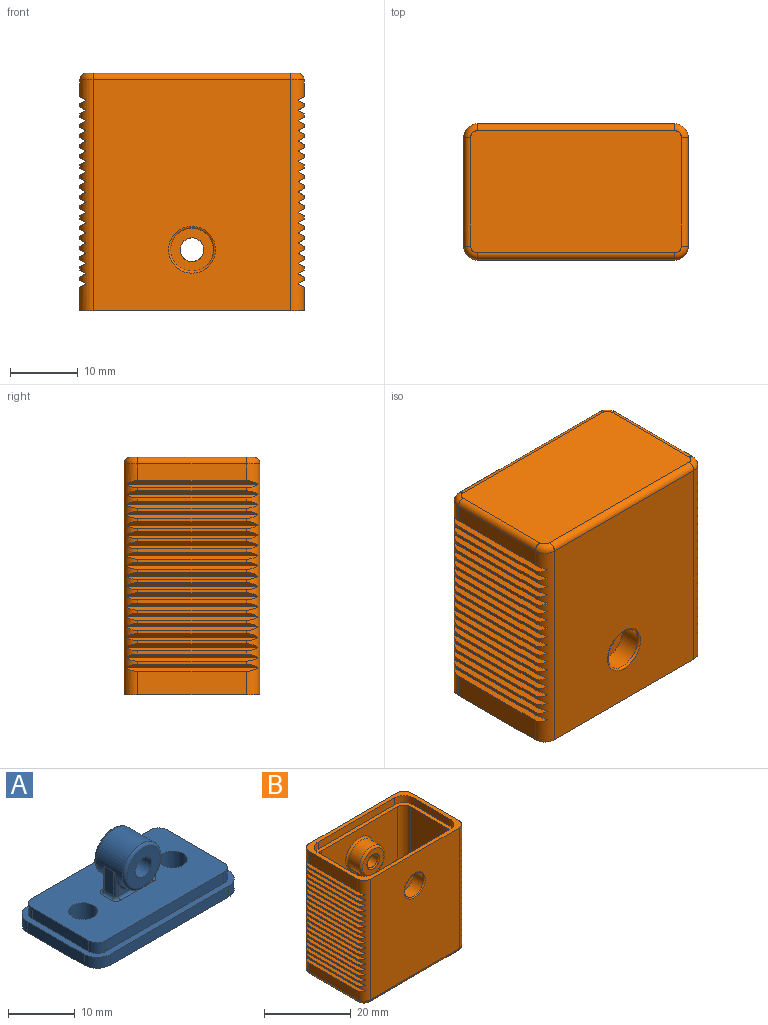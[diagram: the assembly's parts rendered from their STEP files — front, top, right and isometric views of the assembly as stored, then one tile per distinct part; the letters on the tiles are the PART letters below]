
ASSEMBLY  parts=2 mates=1
PART A: 51 faces, bbox 30.6x17.6x13.3 mm
  f0: plane 3.5x1.67mm, normal (0,-1,0), area 1.8mm2, adj f32,f40,f41
  f1: plane 3.5x1.67mm, normal (0,1,0), area 1.8mm2, adj f33,f42,f43
  f2: plane 28.6x15.6mm, normal (0,0,1), area 379.2mm2, adj f9,f10,f11,f12,f25,f26,f27,f28
  f3: plane 30.6x17.6mm, normal (0,0,1), area 88.5mm2, adj f4,f6,f7,f8,f9,f10,f11,f12
  f4: plane 12x2mm, normal (-1,0,0), area 24mm2, adj f3,f5,f21,f23
  f5: plane 30.6x17.6mm, normal (0,0,-1), area 502.8mm2, adj f4,f6,f7,f8,f21,f22,f23,f24
  f6: plane 12x2mm, normal (1,0,0), area 24mm2, adj f3,f5,f22,f24
  f7: plane 25x2mm, normal (0,-1,0), area 50mm2, adj f3,f5,f23,f24
  f8: plane 25x2mm, normal (0,1,0), area 50mm2, adj f3,f5,f21,f22
  f9: plane 12x2mm, normal (-1,0,0), area 24mm2, adj f2,f3,f25,f27
  f10: plane 12x2mm, normal (1,0,0), area 24mm2, adj f2,f3,f26,f28
  f11: plane 25x2mm, normal (0,-1,0), area 50mm2, adj f2,f3,f27,f28
  f12: plane 25x2mm, normal (0,1,0), area 50mm2, adj f2,f3,f25,f26
  f13: plane 4.5x2mm, normal (-1,0,0), area 9mm2, adj f18,f31,f34,f35
  f14: plane 4.5x2mm, normal (1,0,0), area 9mm2, adj f18,f41,f42,f46
  f15: plane 3.5x1.67mm, normal (0,-1,0), area 1.8mm2, adj f31,f32,f40
  f16: plane 3.5x1.67mm, normal (0,1,0), area 1.8mm2, adj f33,f34,f43
  f17: cylinder r=1.75mm len=6.6mm, axis (0,1,0), area 72.6mm2, adj f19,f20
  f18: cylinder r=4mm len=8mm, axis (0,1,0), area 94.7mm2, adj f13,f14,f29,f30,f32,f33,f37,f38
  f19: plane 7x7mm, normal (0,-1,0), area 28.9mm2, adj f17,f48
  f20: plane 7x7mm, normal (0,1,0), area 28.9mm2, adj f17,f47
  f21: cylinder r=2.8mm len=2.8mm, axis (0,0,-1), area 8.8mm2, adj f3,f4,f5,f8
  f22: cylinder r=2.8mm len=2.8mm, axis (0,0,1), area 8.8mm2, adj f3,f5,f6,f8
  f23: cylinder r=2.8mm len=2.8mm, axis (0,0,1), area 8.8mm2, adj f3,f4,f5,f7
  f24: cylinder r=2.8mm len=2.8mm, axis (0,0,-1), area 8.8mm2, adj f3,f5,f6,f7
  f25: cylinder r=1.8mm len=2mm, axis (0,0,-1), area 5.7mm2, adj f2,f3,f9,f12
  f26: cylinder r=1.8mm len=2mm, axis (0,0,1), area 5.7mm2, adj f2,f3,f10,f12
  f27: cylinder r=1.8mm len=2mm, axis (0,0,1), area 5.7mm2, adj f2,f3,f9,f11
  f28: cylinder r=1.8mm len=2mm, axis (0,0,-1), area 5.7mm2, adj f2,f3,f10,f11
  f29: bspline ~2.89x1mm, area 1.1mm2, adj f18,f31,f32
  f30: bspline ~2.89x1mm, area 1.1mm2, adj f18,f33,f34
  f31: cylinder r=0.5mm len=4.5mm, axis (0,0,1), area 2.3mm2, adj f13,f15,f29,f36
  f32: torus R=4.5mm, axis (0,-1,0), area 5.9mm2, adj f0,f15,f18,f29,f37
  f33: torus R=4.5mm, axis (0,-1,0), area 5.9mm2, adj f1,f16,f18,f30,f38
  f34: cylinder r=0.5mm len=4.5mm, axis (0,0,-1), area 2.3mm2, adj f13,f16,f30,f39
  f35: cylinder r=0.5mm len=2mm, axis (0,1,0), area 1.6mm2, adj f2,f13,f36,f39
  f36: torus R=1mm, axis (0,0,1), area 0.8mm2, adj f2,f31,f35,f40
  f37: bspline ~2.89x1mm, area 1.1mm2, adj f18,f32,f41
  f38: bspline ~2.89x1mm, area 1.1mm2, adj f18,f33,f42
  f39: torus R=1mm, axis (0,0,1), area 0.8mm2, adj f2,f34,f35,f43
  f40: cylinder r=0.5mm len=7mm, axis (-1,0,0), area 5.5mm2, adj f0,f2,f15,f36,f44
  f41: cylinder r=0.5mm len=4.5mm, axis (0,0,-1), area 2.3mm2, adj f0,f14,f37,f44
  f42: cylinder r=0.5mm len=4.5mm, axis (0,0,1), area 2.3mm2, adj f1,f14,f38,f45
  f43: cylinder r=0.5mm len=7mm, axis (1,0,0), area 5.5mm2, adj f1,f2,f16,f39,f45
  f44: torus R=1mm, axis (0,0,1), area 0.8mm2, adj f2,f40,f41,f46
  f45: torus R=1mm, axis (0,0,1), area 0.8mm2, adj f2,f42,f43,f46
  f46: cylinder r=0.5mm len=2mm, axis (0,-1,0), area 1.6mm2, adj f2,f14,f44,f45
  f47: torus R=3.5mm, axis (0,-1,0), area 18.8mm2, adj f18,f20
  f48: torus R=3.5mm, axis (0,-1,0), area 18.8mm2, adj f18,f19
  f49: cylinder r=2.15mm len=4.3mm, axis (0,0,-1), area 54mm2, adj f2,f5
  f50: cylinder r=2.15mm len=4.3mm, axis (0,0,-1), area 54mm2, adj f2,f5
PART B: 220 faces, bbox 33.3x20.3x35 mm
  f0: plane 16x0.46mm, normal (1,0,0), area 7.4mm2, adj f38,f39,f209,f211
  f1: plane 16x0.46mm, normal (1,0,0), area 7.4mm2, adj f38,f39,f207,f208
  f2: plane 16x0.46mm, normal (1,0,0), area 7.4mm2, adj f38,f39,f205,f206
  f3: plane 16x0.46mm, normal (1,0,0), area 7.4mm2, adj f38,f39,f203,f204
  f4: plane 16x0.46mm, normal (1,0,0), area 7.4mm2, adj f38,f39,f201,f202
  f5: plane 16x0.46mm, normal (1,0,0), area 7.4mm2, adj f38,f39,f199,f200
  f6: plane 16x0.46mm, normal (1,0,0), area 7.4mm2, adj f38,f39,f197,f198
  f7: plane 16x0.46mm, normal (1,0,0), area 7.4mm2, adj f38,f39,f195,f196
  f8: plane 16x0.46mm, normal (1,0,0), area 7.4mm2, adj f38,f39,f193,f194
  f9: plane 16x0.46mm, normal (1,0,0), area 7.4mm2, adj f38,f39,f191,f192
  f10: plane 16x0.46mm, normal (1,0,0), area 7.4mm2, adj f38,f39,f189,f190
  f11: plane 16x0.46mm, normal (1,0,0), area 7.4mm2, adj f38,f39,f187,f188
  f12: plane 16x0.46mm, normal (1,0,0), area 7.4mm2, adj f38,f39,f185,f186
  f13: plane 16x0.46mm, normal (1,0,0), area 7.4mm2, adj f38,f39,f183,f184
  f14: plane 16x0.46mm, normal (1,0,0), area 7.4mm2, adj f38,f39,f179,f180
  f15: plane 16x0.46mm, normal (1,0,0), area 7.4mm2, adj f38,f39,f177,f178
  f16: plane 16x0.46mm, normal (1,0,0), area 7.4mm2, adj f38,f39,f175,f176
  f17: plane 16x0.46mm, normal (1,0,0), area 7.4mm2, adj f38,f39,f174,f210
  f18: plane 16x2.48mm, normal (1,0,0), area 39.7mm2, adj f38,f39,f182,f215
  f19: plane 16x0.46mm, normal (-1,0,0), area 7.4mm2, adj f40,f41,f171,f173
  f20: plane 16x0.46mm, normal (-1,0,0), area 7.4mm2, adj f40,f41,f169,f170
  f21: plane 16x0.46mm, normal (-1,0,0), area 7.4mm2, adj f40,f41,f167,f168
  f22: plane 16x0.46mm, normal (-1,0,0), area 7.4mm2, adj f40,f41,f165,f166
  f23: plane 16x0.46mm, normal (-1,0,0), area 7.4mm2, adj f40,f41,f163,f164
  f24: plane 16x0.46mm, normal (-1,0,0), area 7.4mm2, adj f40,f41,f161,f162
  f25: plane 16x0.46mm, normal (-1,0,0), area 7.4mm2, adj f40,f41,f159,f160
  f26: plane 16x0.46mm, normal (-1,0,0), area 7.4mm2, adj f40,f41,f157,f158
  f27: plane 16x0.46mm, normal (-1,0,0), area 7.4mm2, adj f40,f41,f155,f156
  f28: plane 16x0.46mm, normal (-1,0,0), area 7.4mm2, adj f40,f41,f153,f154
  f29: plane 16x0.46mm, normal (-1,0,0), area 7.4mm2, adj f40,f41,f151,f152
  f30: plane 16x0.46mm, normal (-1,0,0), area 7.4mm2, adj f40,f41,f149,f150
  f31: plane 16x0.46mm, normal (-1,0,0), area 7.4mm2, adj f40,f41,f147,f148
  f32: plane 16x0.46mm, normal (-1,0,0), area 7.4mm2, adj f40,f41,f145,f146
  f33: plane 16x0.46mm, normal (-1,0,0), area 7.4mm2, adj f40,f41,f143,f144
  f34: plane 16x0.46mm, normal (-1,0,0), area 7.4mm2, adj f40,f41,f141,f142
  f35: plane 16x0.46mm, normal (-1,0,0), area 7.4mm2, adj f40,f41,f139,f140
  f36: plane 16x0.46mm, normal (-1,0,0), area 7.4mm2, adj f40,f41,f137,f138
  f37: plane 16x3.48mm, normal (-1,0,0), area 55.7mm2, adj f40,f41,f54,f136
  f38: cylinder r=2mm len=34mm, axis (0,0,-1), area 81.2mm2, adj f0,f1,f2,f3,f4,f5,f6,f7
  f39: cylinder r=2mm len=34mm, axis (0,0,1), area 81.2mm2, adj f0,f1,f2,f3,f4,f5,f6,f7
  f40: cylinder r=2mm len=34mm, axis (0,0,-1), area 81.2mm2, adj f19,f20,f21,f22,f23,f24,f25,f26
  f41: cylinder r=2mm len=34mm, axis (0,0,1), area 81.2mm2, adj f19,f20,f21,f22,f23,f24,f25,f26
  f42: plane 29x25mm, normal (0,-1,0), area 648.5mm2, adj f47,f49,f65,f92,f93,f108,f109,f110
  f43: plane 29x25mm, normal (0,1,0), area 648.5mm2, adj f46,f48,f62,f91,f93,f122,f123,f124
  f44: plane 29x12mm, normal (-1,0,0), area 348mm2, adj f46,f47,f61,f93
  f45: plane 29x12mm, normal (1,0,0), area 348mm2, adj f48,f49,f66,f93
  f46: cylinder r=2mm len=29mm, axis (0,0,1), area 91.1mm2, adj f43,f44,f60,f93
  f47: cylinder r=2mm len=29mm, axis (0,0,-1), area 91.1mm2, adj f42,f44,f63,f93
  f48: cylinder r=2mm len=29mm, axis (0,0,-1), area 91.1mm2, adj f43,f45,f64,f93
  f49: cylinder r=2mm len=29mm, axis (0,0,1), area 91.1mm2, adj f42,f45,f67,f93
  f50: cylinder r=1.75mm len=3.5mm, axis (0,-1,0), area 29.7mm2, adj f69,f80
  f51: cylinder r=4mm len=8mm, axis (0,-1,0), area 76.2mm2, adj f89,f91,f130,f131,f133,f134,f135
  f52: plane 34x29mm, normal (0,1,0), area 952.7mm2, adj f39,f40,f54,f82,f83,f84,f85,f86
  f53: cylinder r=1.75mm len=3.7mm, axis (0,-1,0), area 40.7mm2, adj f77,f81
  f54: plane 33x20mm, normal (0,0,1), area 106.3mm2, adj f37,f38,f39,f40,f41,f52,f55,f56
  f55: plane 34x29mm, normal (0,-1,0), area 948.6mm2, adj f38,f41,f54,f88,f219
  f56: plane 16x3.48mm, normal (1,0,0), area 55.7mm2, adj f38,f39,f54,f181
  f57: plane 16x2.48mm, normal (-1,0,0), area 39.7mm2, adj f40,f41,f172,f216
  f58: plane 31x18mm, normal (0,0,-1), area 557.1mm2, adj f212,f213,f214,f215,f216,f217,f218,f219
  f59: plane 25x12mm, normal (0,0,1), area 300mm2, adj f61,f62,f65,f66
  f60: sphere r=2mm, area 6.3mm2, adj f46,f61,f62
  f61: cylinder r=2mm len=12mm, axis (0,-1,0), area 37.7mm2, adj f44,f59,f60,f63
  f62: cylinder r=2mm len=25mm, axis (-1,0,0), area 78.5mm2, adj f43,f59,f60,f64
  f63: sphere r=2mm, area 6.3mm2, adj f47,f61,f65
  f64: sphere r=2mm, area 6.3mm2, adj f48,f62,f66
  f65: cylinder r=2mm len=25mm, axis (1,0,0), area 78.5mm2, adj f42,f59,f63,f67
  f66: cylinder r=2mm len=12mm, axis (0,1,0), area 37.7mm2, adj f45,f59,f64,f67
  f67: sphere r=2mm, area 6.3mm2, adj f49,f65,f66
  f68: cylinder r=4mm len=8mm, axis (0,-1,0), area 76.2mm2, adj f90,f92,f116,f117,f119,f120,f121
  f69: plane 6.3x6.3mm, normal (0,-1,0), area 21.6mm2, adj f50,f70
  f70: cylinder r=3.15mm len=6.3mm, axis (0,-1,0), area 63.3mm2, adj f69,f88
  f71: plane 2.8x2.2mm, normal (0.87,0,0.5), area 7.1mm2, adj f72,f76,f77,f85
  f72: plane 2.8x2.2mm, normal (0.87,0,-0.5), area 7.1mm2, adj f71,f73,f77,f83
  f73: plane 3.23x2.2mm, normal (0,0,-1), area 7.1mm2, adj f72,f74,f77,f82
  f74: plane 2.8x2.2mm, normal (-0.87,0,-0.5), area 7.1mm2, adj f73,f75,f77,f84
  f75: plane 2.8x2.2mm, normal (-0.87,0,0.5), area 7.1mm2, adj f74,f76,f77,f86
  f76: plane 3.23x2.2mm, normal (0,0,1), area 7.1mm2, adj f71,f75,f77,f87
  f77: plane 6.47x5.6mm, normal (0,1,0), area 17.5mm2, adj f53,f71,f72,f73,f74,f75,f76
  f78: plane 7x7mm, normal (0,-1,0), area 25.3mm2, adj f81,f90
  f79: plane 7x7mm, normal (0,1,0), area 25.3mm2, adj f80,f89
  f80: torus R=2.05mm, axis (0,1,0), area 5.5mm2, adj f50,f79
  f81: torus R=2.05mm, axis (0,1,0), area 5.5mm2, adj f53,f78
  f82: cylinder r=0.3mm len=3.58mm, axis (1,0,0), area 1.6mm2, adj f52,f73,f83,f84
  f83: cylinder r=0.3mm len=3.25mm, axis (0.5,0,0.87), area 1.6mm2, adj f52,f72,f82,f85
  f84: cylinder r=0.3mm len=3.25mm, axis (0.5,0,-0.87), area 1.6mm2, adj f52,f74,f82,f86
  f85: cylinder r=0.3mm len=3.25mm, axis (-0.5,0,0.87), area 1.6mm2, adj f52,f71,f83,f87
  f86: cylinder r=0.3mm len=3.25mm, axis (-0.5,0,-0.87), area 1.6mm2, adj f52,f75,f84,f87
  f87: cylinder r=0.3mm len=3.58mm, axis (-1,0,0), area 1.6mm2, adj f52,f76,f85,f86
  f88: torus R=3.45mm, axis (0,-1,0), area 9.6mm2, adj f55,f70
  f89: torus R=3.5mm, axis (0,1,0), area 18.8mm2, adj f51,f79
  f90: torus R=3.5mm, axis (0,1,0), area 18.8mm2, adj f68,f78
  f91: torus R=4.5mm, axis (0,-1,0), area 17.6mm2, adj f43,f51,f126,f127
  f92: torus R=4.5mm, axis (0,-1,0), area 17.6mm2, adj f42,f68,f112,f113
  f93: plane 31x18mm, normal (0,0,1), area 89.7mm2, adj f42,f43,f44,f45,f46,f47,f48,f49
  f94: plane 25x2mm, normal (0,1,0), area 50mm2, adj f54,f93,f95,f101
  f95: cylinder r=3mm len=3mm, axis (0,0,1), area 9.4mm2, adj f54,f93,f94,f96
  f96: plane 12x2mm, normal (-1,0,0), area 24mm2, adj f54,f93,f95,f97
  f97: cylinder r=3mm len=3mm, axis (0,0,1), area 9.4mm2, adj f54,f93,f96,f98
  f98: plane 25x2mm, normal (0,-1,0), area 50mm2, adj f54,f93,f97,f99
  f99: cylinder r=3mm len=3mm, axis (0,0,1), area 9.4mm2, adj f54,f93,f98,f100
  f100: plane 12x2mm, normal (1,0,0), area 24mm2, adj f54,f93,f99,f101
  f101: cylinder r=3mm len=3mm, axis (0,0,1), area 9.4mm2, adj f54,f93,f94,f100
  f102: plane 3.32x3.32mm, normal (0,0.71,-0.71), area 9.2mm2, adj f124,f129,f132,f135
  f103: plane 2.26x2.26mm, normal (1,0,0), area 2.6mm2, adj f122,f129,f130
  f104: plane 2.26x2.26mm, normal (-1,0,0), area 2.6mm2, adj f123,f131,f132
  f105: plane 3.32x3.32mm, normal (0,-0.71,-0.71), area 9.2mm2, adj f110,f115,f118,f121
  f106: plane 2.26x2.26mm, normal (1,0,0), area 2.6mm2, adj f109,f117,f118
  f107: plane 2.26x2.26mm, normal (-1,0,0), area 2.6mm2, adj f108,f115,f116
  f108: cylinder r=0.5mm len=2.26mm, axis (0,0,1), area 1.8mm2, adj f42,f107,f111,f112
  f109: cylinder r=0.5mm len=2.26mm, axis (0,0,-1), area 1.8mm2, adj f42,f106,f113,f114
  f110: cylinder r=0.5mm len=2mm, axis (-1,0,0), area 0.8mm2, adj f42,f105,f111,f114
  f111: bspline ~1.66x1mm, area 0.9mm2, adj f42,f108,f110,f115
  f112: sphere r=0.5mm, area 0.3mm2, adj f92,f108,f116
  f113: sphere r=0.5mm, area 0.3mm2, adj f92,f109,f117
  f114: bspline ~1.66x1.17mm, area 0.9mm2, adj f42,f109,f110,f118
  f115: cylinder r=0.5mm len=3.73mm, axis (0,0.71,-0.71), area 3.3mm2, adj f105,f107,f111,f119
  f116: cylinder r=0.5mm len=2.26mm, axis (0,-1,0), area 1.3mm2, adj f68,f107,f112,f119
  f117: cylinder r=0.5mm len=2.26mm, axis (0,-1,0), area 1.3mm2, adj f68,f106,f113,f120
  f118: cylinder r=0.5mm len=3.73mm, axis (0,-0.71,0.71), area 3.3mm2, adj f105,f106,f114,f120
  f119: bspline ~1.54x0.99mm, area 0.6mm2, adj f68,f115,f116,f121
  f120: bspline ~1.19x1.06mm, area 0.6mm2, adj f68,f117,f118,f121
  f121: bspline ~2x0.47mm, area 0.8mm2, adj f68,f105,f119,f120
  f122: cylinder r=0.5mm len=2.26mm, axis (0,0,1), area 1.8mm2, adj f43,f103,f125,f126
  f123: cylinder r=0.5mm len=2.26mm, axis (0,0,-1), area 1.8mm2, adj f43,f104,f127,f128
  f124: cylinder r=0.5mm len=2mm, axis (1,0,0), area 0.8mm2, adj f43,f102,f125,f128
  f125: bspline ~1.66x1mm, area 0.9mm2, adj f43,f122,f124,f129
  f126: sphere r=0.5mm, area 0.3mm2, adj f91,f122,f130
  f127: sphere r=0.5mm, area 0.3mm2, adj f91,f123,f131
  f128: bspline ~1.66x1.04mm, area 0.9mm2, adj f43,f123,f124,f132
  f129: cylinder r=0.5mm len=3.73mm, axis (0,-0.71,-0.71), area 3.3mm2, adj f102,f103,f125,f133
  f130: cylinder r=0.5mm len=2.26mm, axis (0,-1,0), area 1.3mm2, adj f51,f103,f126,f133
  f131: cylinder r=0.5mm len=2.26mm, axis (0,-1,0), area 1.3mm2, adj f51,f104,f127,f134
  f132: cylinder r=0.5mm len=3.73mm, axis (0,0.71,0.71), area 3.3mm2, adj f102,f104,f128,f134
  f133: bspline ~1.54x0.99mm, area 0.6mm2, adj f51,f129,f130,f135
  f134: bspline ~1.19x1.06mm, area 0.6mm2, adj f51,f131,f132,f135
  f135: bspline ~2x0.47mm, area 0.8mm2, adj f51,f102,f133,f134
  f136: plane 19.34x0.9mm, normal (-0.5,0,-0.87), area 19.1mm2, adj f37,f40,f41,f137
  f137: plane 19.34x0.9mm, normal (-0.5,0,0.87), area 19.1mm2, adj f36,f40,f41,f136
  f138: plane 19.34x0.9mm, normal (-0.5,0,-0.87), area 19.1mm2, adj f36,f40,f41,f139
  f139: plane 19.34x0.9mm, normal (-0.5,0,0.87), area 19.1mm2, adj f35,f40,f41,f138
  f140: plane 19.34x0.9mm, normal (-0.5,0,-0.87), area 19.1mm2, adj f35,f40,f41,f141
  f141: plane 19.34x0.9mm, normal (-0.5,0,0.87), area 19.1mm2, adj f34,f40,f41,f140
  f142: plane 19.34x0.9mm, normal (-0.5,0,-0.87), area 19.1mm2, adj f34,f40,f41,f143
  f143: plane 19.34x0.9mm, normal (-0.5,0,0.87), area 19.1mm2, adj f33,f40,f41,f142
  f144: plane 19.34x0.9mm, normal (-0.5,0,-0.87), area 19.1mm2, adj f33,f40,f41,f145
  f145: plane 19.34x0.9mm, normal (-0.5,0,0.87), area 19.1mm2, adj f32,f40,f41,f144
  f146: plane 19.34x0.9mm, normal (-0.5,0,-0.87), area 19.1mm2, adj f32,f40,f41,f147
  f147: plane 19.34x0.9mm, normal (-0.5,0,0.87), area 19.1mm2, adj f31,f40,f41,f146
  f148: plane 19.34x0.9mm, normal (-0.5,0,-0.87), area 19.1mm2, adj f31,f40,f41,f149
  f149: plane 19.34x0.9mm, normal (-0.5,0,0.87), area 19.1mm2, adj f30,f40,f41,f148
  f150: plane 19.34x0.9mm, normal (-0.5,0,-0.87), area 19.1mm2, adj f30,f40,f41,f151
  f151: plane 19.34x0.9mm, normal (-0.5,0,0.87), area 19.1mm2, adj f29,f40,f41,f150
  f152: plane 19.34x0.9mm, normal (-0.5,0,-0.87), area 19.1mm2, adj f29,f40,f41,f153
  f153: plane 19.34x0.9mm, normal (-0.5,0,0.87), area 19.1mm2, adj f28,f40,f41,f152
  f154: plane 19.34x0.9mm, normal (-0.5,0,-0.87), area 19.1mm2, adj f28,f40,f41,f155
  f155: plane 19.34x0.9mm, normal (-0.5,0,0.87), area 19.1mm2, adj f27,f40,f41,f154
  f156: plane 19.34x0.9mm, normal (-0.5,0,-0.87), area 19.1mm2, adj f27,f40,f41,f157
  f157: plane 19.34x0.9mm, normal (-0.5,0,0.87), area 19.1mm2, adj f26,f40,f41,f156
  f158: plane 19.34x0.9mm, normal (-0.5,0,-0.87), area 19.1mm2, adj f26,f40,f41,f159
  f159: plane 19.34x0.9mm, normal (-0.5,0,0.87), area 19.1mm2, adj f25,f40,f41,f158
  f160: plane 19.34x0.9mm, normal (-0.5,0,-0.87), area 19.1mm2, adj f25,f40,f41,f161
  f161: plane 19.34x0.9mm, normal (-0.5,0,0.87), area 19.1mm2, adj f24,f40,f41,f160
  f162: plane 19.34x0.9mm, normal (-0.5,0,-0.87), area 19.1mm2, adj f24,f40,f41,f163
  f163: plane 19.34x0.9mm, normal (-0.5,0,0.87), area 19.1mm2, adj f23,f40,f41,f162
  f164: plane 19.34x0.9mm, normal (-0.5,0,-0.87), area 19.1mm2, adj f23,f40,f41,f165
  f165: plane 19.34x0.9mm, normal (-0.5,0,0.87), area 19.1mm2, adj f22,f40,f41,f164
  f166: plane 19.34x0.9mm, normal (-0.5,0,-0.87), area 19.1mm2, adj f22,f40,f41,f167
  f167: plane 19.34x0.9mm, normal (-0.5,0,0.87), area 19.1mm2, adj f21,f40,f41,f166
  f168: plane 19.34x0.9mm, normal (-0.5,0,-0.87), area 19.1mm2, adj f21,f40,f41,f169
  f169: plane 19.34x0.9mm, normal (-0.5,0,0.87), area 19.1mm2, adj f20,f40,f41,f168
  f170: plane 19.34x0.9mm, normal (-0.5,0,-0.87), area 19.1mm2, adj f20,f40,f41,f171
  f171: plane 19.34x0.9mm, normal (-0.5,0,0.87), area 19.1mm2, adj f19,f40,f41,f170
  f172: plane 19.34x0.9mm, normal (-0.5,0,0.87), area 19.1mm2, adj f40,f41,f57,f173
  f173: plane 19.34x0.9mm, normal (-0.5,0,-0.87), area 19.1mm2, adj f19,f40,f41,f172
  f174: plane 19.34x0.9mm, normal (0.5,0,0.87), area 19.1mm2, adj f17,f38,f39,f175
  f175: plane 19.34x0.9mm, normal (0.5,0,-0.87), area 19.1mm2, adj f16,f38,f39,f174
  f176: plane 19.34x0.9mm, normal (0.5,0,0.87), area 19.1mm2, adj f16,f38,f39,f177
  f177: plane 19.34x0.9mm, normal (0.5,0,-0.87), area 19.1mm2, adj f15,f38,f39,f176
  f178: plane 19.34x0.9mm, normal (0.5,0,0.87), area 19.1mm2, adj f15,f38,f39,f179
  f179: plane 19.34x0.9mm, normal (0.5,0,-0.87), area 19.1mm2, adj f14,f38,f39,f178
  f180: plane 19.34x0.9mm, normal (0.5,0,0.87), area 19.1mm2, adj f14,f38,f39,f181
  f181: plane 19.34x0.9mm, normal (0.5,0,-0.87), area 19.1mm2, adj f38,f39,f56,f180
  f182: plane 19.34x0.9mm, normal (0.5,0,0.87), area 19.1mm2, adj f18,f38,f39,f183
  f183: plane 19.34x0.9mm, normal (0.5,0,-0.87), area 19.1mm2, adj f13,f38,f39,f182
  f184: plane 19.34x0.9mm, normal (0.5,0,0.87), area 19.1mm2, adj f13,f38,f39,f185
  f185: plane 19.34x0.9mm, normal (0.5,0,-0.87), area 19.1mm2, adj f12,f38,f39,f184
  f186: plane 19.34x0.9mm, normal (0.5,0,0.87), area 19.1mm2, adj f12,f38,f39,f187
  f187: plane 19.34x0.9mm, normal (0.5,0,-0.87), area 19.1mm2, adj f11,f38,f39,f186
  f188: plane 19.34x0.9mm, normal (0.5,0,0.87), area 19.1mm2, adj f11,f38,f39,f189
  f189: plane 19.34x0.9mm, normal (0.5,0,-0.87), area 19.1mm2, adj f10,f38,f39,f188
  f190: plane 19.34x0.9mm, normal (0.5,0,0.87), area 19.1mm2, adj f10,f38,f39,f191
  f191: plane 19.34x0.9mm, normal (0.5,0,-0.87), area 19.1mm2, adj f9,f38,f39,f190
  f192: plane 19.34x0.9mm, normal (0.5,0,0.87), area 19.1mm2, adj f9,f38,f39,f193
  f193: plane 19.34x0.9mm, normal (0.5,0,-0.87), area 19.1mm2, adj f8,f38,f39,f192
  f194: plane 19.34x0.9mm, normal (0.5,0,0.87), area 19.1mm2, adj f8,f38,f39,f195
  f195: plane 19.34x0.9mm, normal (0.5,0,-0.87), area 19.1mm2, adj f7,f38,f39,f194
  f196: plane 19.34x0.9mm, normal (0.5,0,0.87), area 19.1mm2, adj f7,f38,f39,f197
  f197: plane 19.34x0.9mm, normal (0.5,0,-0.87), area 19.1mm2, adj f6,f38,f39,f196
  f198: plane 19.34x0.9mm, normal (0.5,0,0.87), area 19.1mm2, adj f6,f38,f39,f199
  f199: plane 19.34x0.9mm, normal (0.5,0,-0.87), area 19.1mm2, adj f5,f38,f39,f198
  f200: plane 19.34x0.9mm, normal (0.5,0,0.87), area 19.1mm2, adj f5,f38,f39,f201
  f201: plane 19.34x0.9mm, normal (0.5,0,-0.87), area 19.1mm2, adj f4,f38,f39,f200
  f202: plane 19.34x0.9mm, normal (0.5,0,0.87), area 19.1mm2, adj f4,f38,f39,f203
  f203: plane 19.34x0.9mm, normal (0.5,0,-0.87), area 19.1mm2, adj f3,f38,f39,f202
  f204: plane 19.34x0.9mm, normal (0.5,0,0.87), area 19.1mm2, adj f3,f38,f39,f205
  f205: plane 19.34x0.9mm, normal (0.5,0,-0.87), area 19.1mm2, adj f2,f38,f39,f204
  f206: plane 19.34x0.9mm, normal (0.5,0,0.87), area 19.1mm2, adj f2,f38,f39,f207
  f207: plane 19.34x0.9mm, normal (0.5,0,-0.87), area 19.1mm2, adj f1,f38,f39,f206
  f208: plane 19.34x0.9mm, normal (0.5,0,0.87), area 19.1mm2, adj f1,f38,f39,f209
  f209: plane 19.34x0.9mm, normal (0.5,0,-0.87), area 19.1mm2, adj f0,f38,f39,f208
  f210: plane 19.34x0.9mm, normal (0.5,0,-0.87), area 19.1mm2, adj f17,f38,f39,f211
  f211: plane 19.34x0.9mm, normal (0.5,0,0.87), area 19.1mm2, adj f0,f38,f39,f210
  f212: cylinder r=1mm len=29mm, axis (-1,0,0), area 45.6mm2, adj f52,f58,f213,f214
  f213: torus R=1mm, axis (0,0,1), area 4mm2, adj f39,f58,f212,f215
  f214: torus R=1mm, axis (0,0,1), area 4mm2, adj f40,f58,f212,f216
  f215: cylinder r=1mm len=16mm, axis (0,1,0), area 25.1mm2, adj f18,f58,f213,f217
  f216: cylinder r=1mm len=16mm, axis (0,-1,0), area 25.1mm2, adj f57,f58,f214,f218
  f217: torus R=1mm, axis (0,0,1), area 4mm2, adj f38,f58,f215,f219
  f218: torus R=1mm, axis (0,0,1), area 4mm2, adj f41,f58,f216,f219
  f219: cylinder r=1mm len=29mm, axis (1,0,0), area 45.6mm2, adj f55,f58,f217,f218
PLACE A t=(9.5,0,1)mm
PLACE B rot(axis=(0,1,0),180deg) t=(9.5,0,35)mm
MATE slider A.f5 <-> B.f58  axis (0,0,-1) through (9.5,0,0)mm
